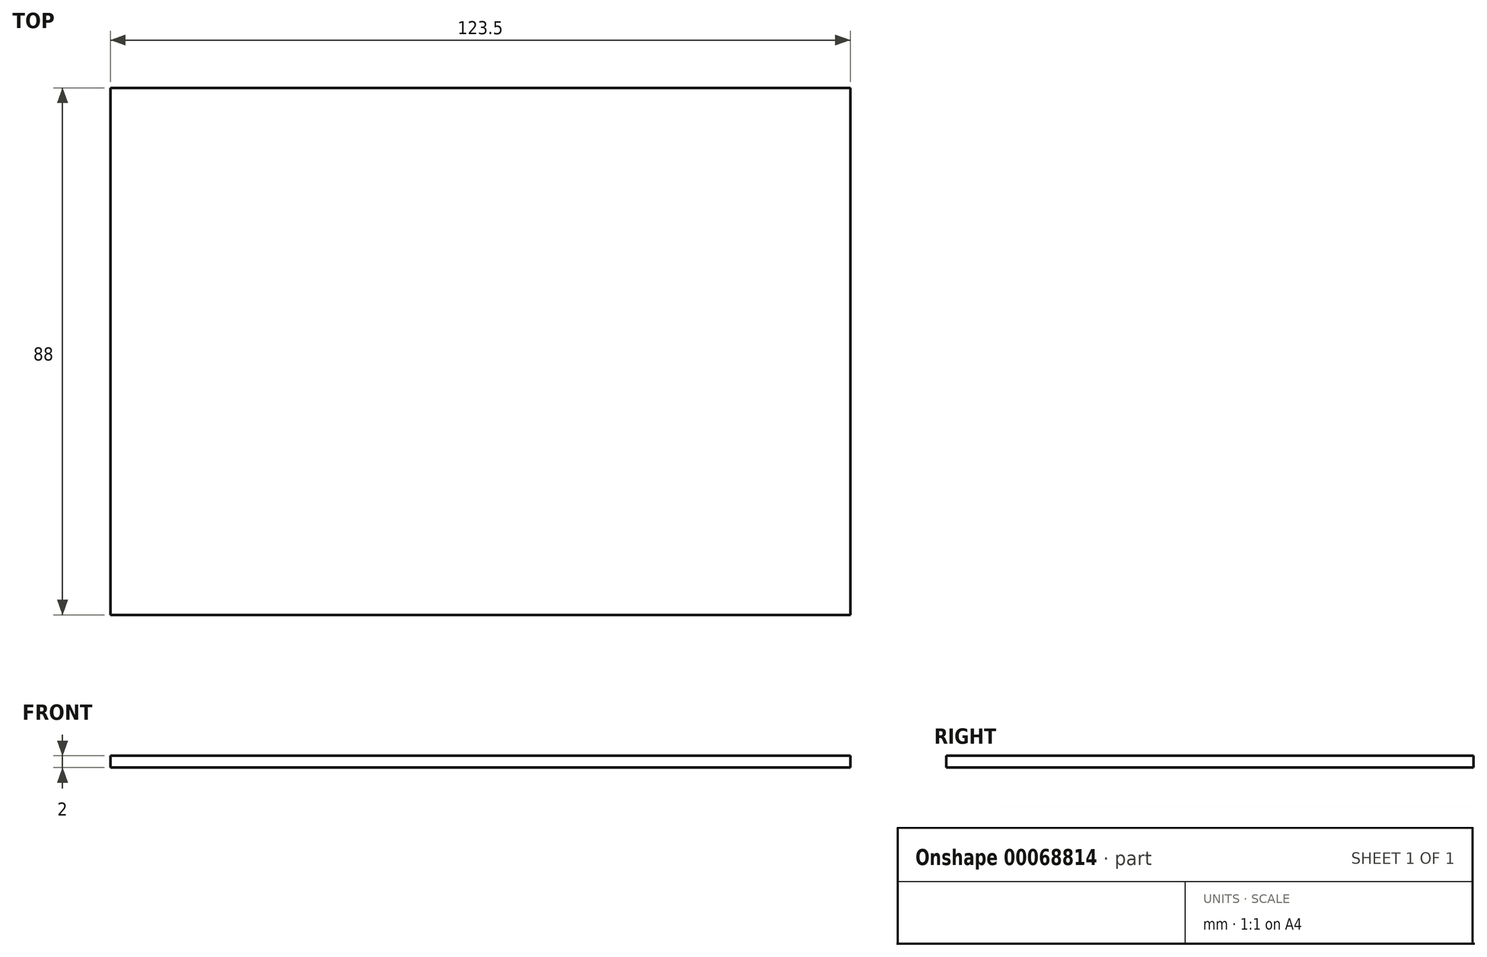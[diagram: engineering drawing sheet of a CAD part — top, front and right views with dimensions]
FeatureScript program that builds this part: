
annotation { "Feature Type Name" : "Feature", "Feature Type Description" : "" }
export const myFeature = defineFeature(function(context is Context, id is Id, definition is map)
    precondition{}
    {
        {
            var Q0;
            Q0=qCreatedBy(makeId("Top.planeOp"),FACE);
            var sketch = newSketch(context, id + "F0", { "sketchPlane" : qUnion([Q0])});
            skLineSegment(sketch, "E0.rect.bottom", {"start": v(61.75, 44) * mm, "end": v(-61.75, 44) * mm});
            skLineSegment(sketch, "E0.rect.top", {"start": v(61.75, -44) * mm, "end": v(-61.75, -44) * mm});
            skLineSegment(sketch, "E0.rect.left", {"start": v(61.75, 44) * mm, "end": v(61.75, -44) * mm});
            skLineSegment(sketch, "E0.rect.right", {"start": v(-61.75, 44) * mm, "end": v(-61.75, -44) * mm});
            skPoint(sketch, "E0.rect.middle", {"position": v(0, 0) * mm});
            skSolve(sketch);
        }
        {
            var Q0;
            Q0 = qSketchRegion(id + "F0", true);
            extrude(context, id + "F1", {"entities" : qUnion([Q0]), "depth" : 2 * mm});
        }
    });
